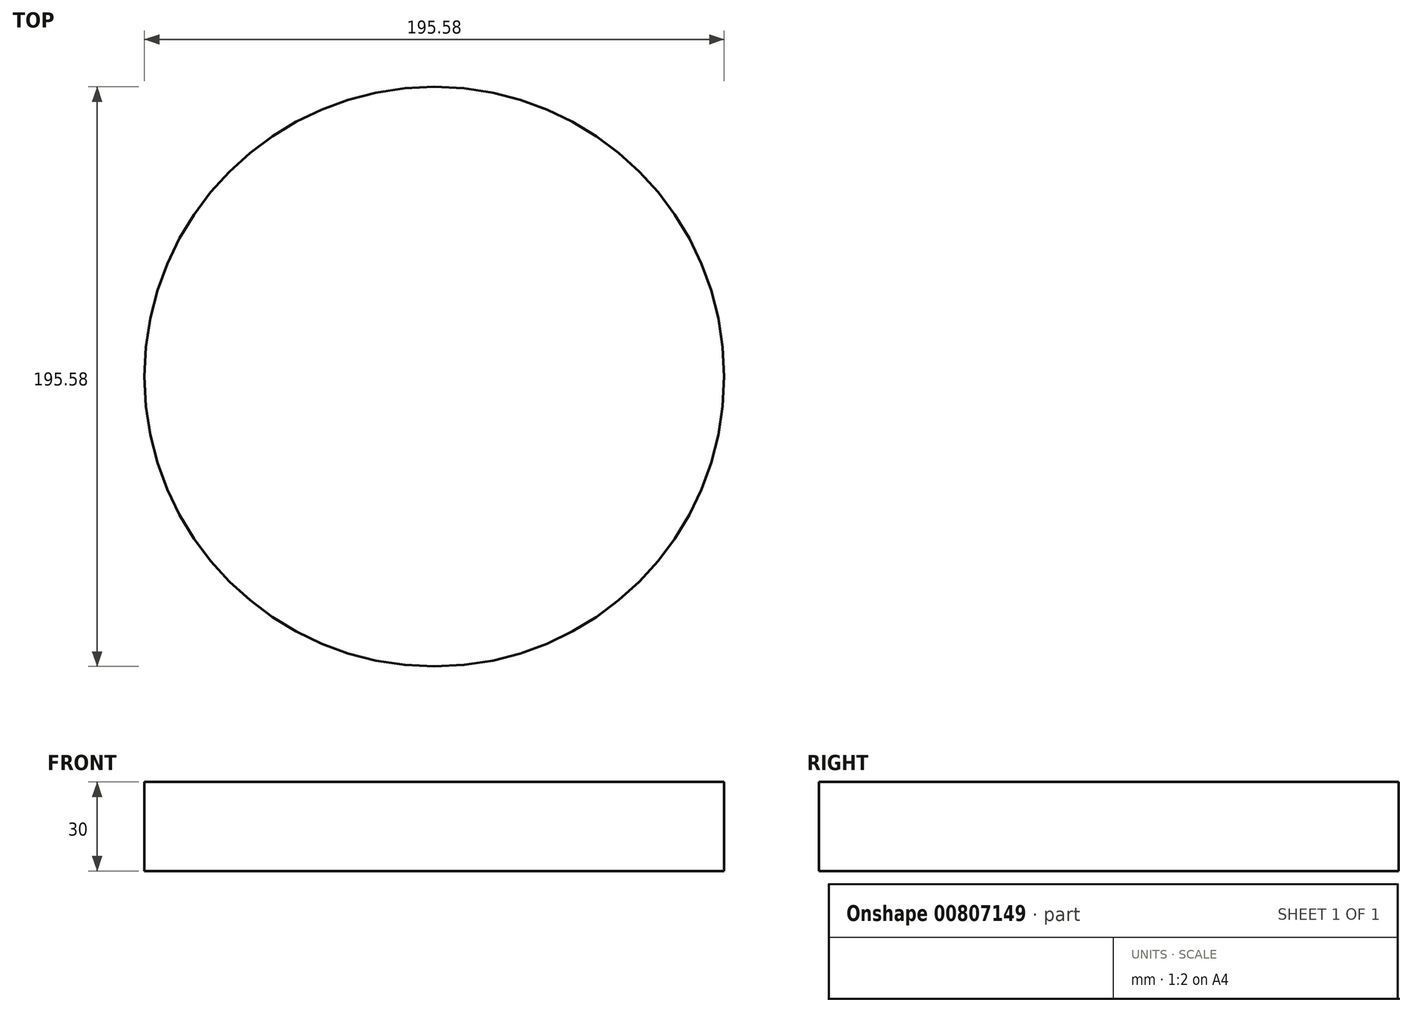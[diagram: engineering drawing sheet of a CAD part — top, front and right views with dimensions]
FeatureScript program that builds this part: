
annotation { "Feature Type Name" : "Feature", "Feature Type Description" : "" }
export const myFeature = defineFeature(function(context is Context, id is Id, definition is map)
    precondition{}
    {
        {
            var Q0;
            Q0=qCreatedBy(makeId("Top.planeOp"),FACE);
            var sketch = newSketch(context, id + "F0", { "sketchPlane" : qUnion([Q0])});
            skCircle(sketch, "E0", {"center": v(0, 0) * mm, "radius": 97.8 * mm});
            skSolve(sketch);
        }
        {
            var Q0;
            Q0 = qSketchRegion(id + "F0", true);
            extrude(context, id + "F1", {"entities" : qUnion([Q0]), "depth" : 30 * mm, "offsetDistance" : 25.4 * mm});
        }
    });
